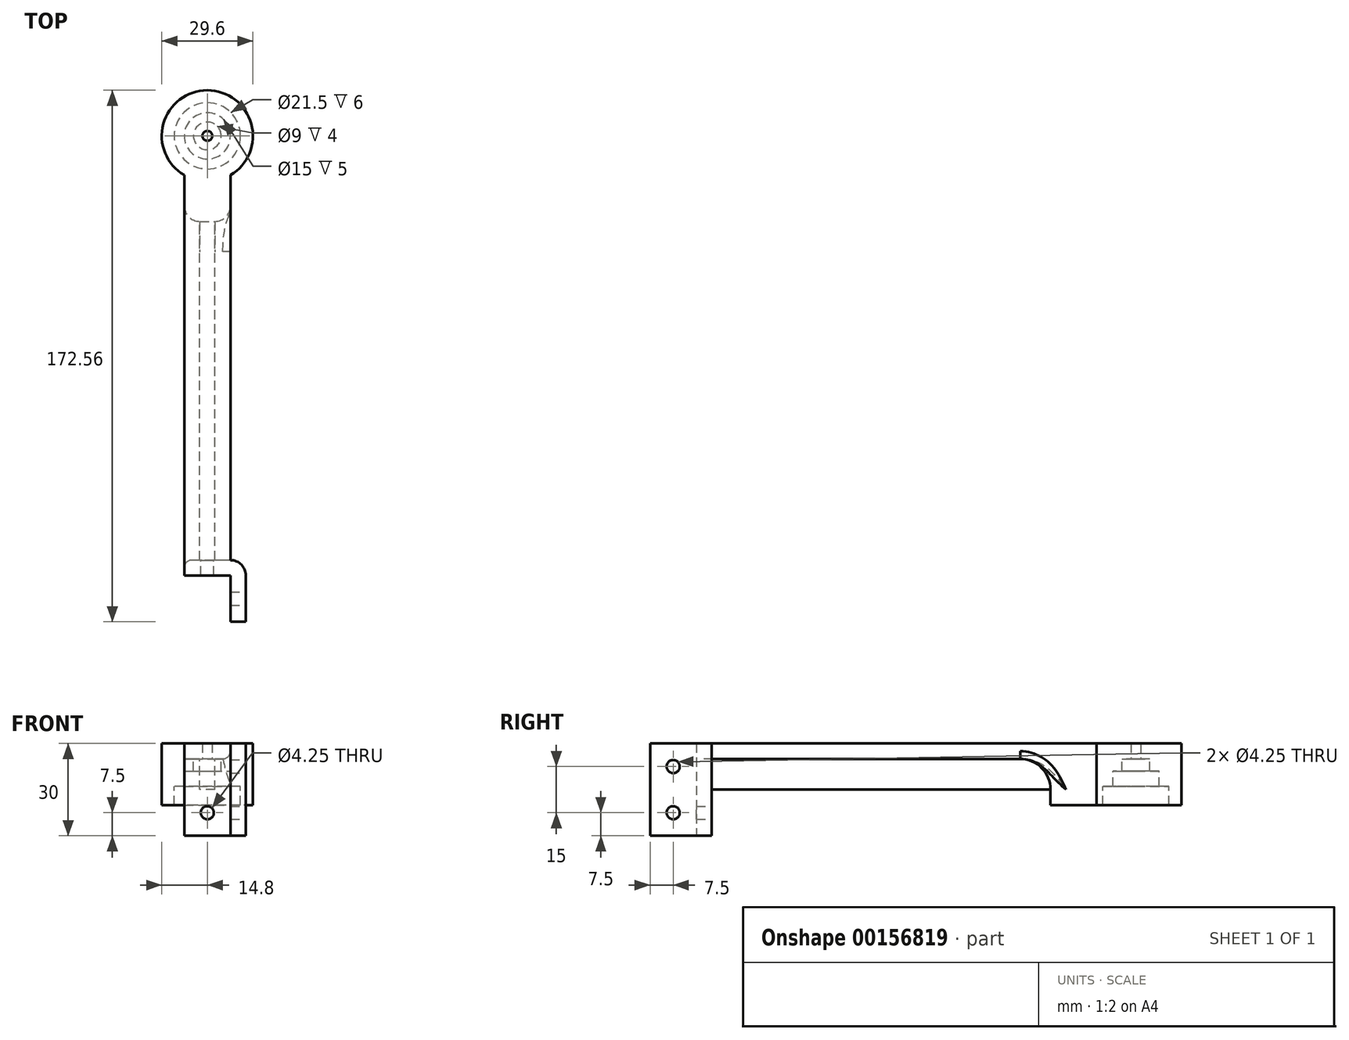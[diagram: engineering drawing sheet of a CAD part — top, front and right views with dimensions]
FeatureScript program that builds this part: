
annotation { "Feature Type Name" : "Feature", "Feature Type Description" : "" }
export const myFeature = defineFeature(function(context is Context, id is Id, definition is map)
    precondition{}
    {
        {
            var Q0;
            Q0=qCreatedBy(makeId("Top.planeOp"),FACE);
            var sketch = newSketch(context, id + "F0", { "sketchPlane" : qUnion([Q0])});
            skLineSegment(sketch, "E0.top", {"start": v(7.5, -65) * mm, "end": v(-7.5, -65) * mm});
            skLineSegment(sketch, "E0.left", {"start": v(7.5, 65) * mm, "end": v(7.5, -65) * mm});
            skLineSegment(sketch, "E0.right", {"start": v(-7.5, 65) * mm, "end": v(-7.5, -65) * mm});
            skPoint(sketch, "E0.middle", {"position": v(0, 0) * mm});
            skArc(sketch, "E1", {"start": v(10, 77.76) * mm, "mid": v(0, 67.76) * mm, "end": v(-10, 77.76) * mm, "construction": true});
            skArc(sketch, "E2", {"start": v(14.8, 77.76) * mm, "mid": v(12.85, 70.4) * mm, "end": v(7.5, 65) * mm});
            skArc(sketch, "E3.trimOffspring", {"start": v(-7.5, 65) * mm, "mid": v(-12.85, 70.4) * mm, "end": v(-14.8, 77.76) * mm});
            skArc(sketch, "E4", {"start": v(14.8, 77.76) * mm, "mid": v(0, 92.56) * mm, "end": v(-14.8, 77.76) * mm});
            skArc(sketch, "E5", {"start": v(10, 77.76) * mm, "mid": v(0, 87.76) * mm, "end": v(-10, 77.76) * mm, "construction": true});
            skCircle(sketch, "E6", {"center": v(0, 77.76) * mm, "radius": 1.6 * mm});
            skSolve(sketch);
        }
        {
            var Q0;
            Q0=qSketchRegion(id+"F0",true);
            extrude(context, id + "F1", {"entities" : qUnion([Q0]), "depth" : 5 * mm});
        }
        {
            var Q0;
            Q0=makeQuery(id+"F1.opExtrude","CAP_FACE",FACE,{"disambiguationData":[OSD([sQuery(id+"F0.wireOp",EDGE,"E0.top"),sQuery(id+"F0.wireOp",EDGE,"E0.left"),sQuery(id+"F0.wireOp",EDGE,"E0.right"),sQuery(id+"F0.wireOp",EDGE,"E1"),sQuery(id+"F0.wireOp",EDGE,"E2"),sQuery(id+"F0.wireOp",EDGE,"PIiDe5xE-f48K-SFec-VeXW-8BEBNLWFIkbi"),sQuery(id+"F0.wireOp",EDGE,"eIUL9qrP-yxCU-yPW2-WiAL-nEhhlfbeueWp"),sQuery(id+"F0.wireOp",EDGE,"NGNwJRk0-PCto-h1U5-63Ki-JEH3zZtKr13U"),sQuery(id+"F0.wireOp",EDGE,"9JBDCSfi-IbL8-SLhU-QHty-wRifAwfVzchu"),sQuery(id+"F0.wireOp",EDGE,"uUBvHsI4-013N-H5fo-1cTm-d3MeMkX9Puon"),sQuery(id+"F0.wireOp",EDGE,"XBA7hVCw-AGae-m0qZ-7ZIr-1CJPmpSNLz33"),sQuery(id+"F0.wireOp",EDGE,"E3.trimOffspring")])],"isStart":false});
            var sketch = newSketch(context, id + "F2", { "sketchPlane" : qUnion([Q0])});
            skLineSegment(sketch, "E7.bottom", {"start": v(2.5, -65) * mm, "end": v(-2.5, -65) * mm});
            skLineSegment(sketch, "E7.top", {"start": v(2.5, 65) * mm, "end": v(-2.5, 65) * mm});
            skLineSegment(sketch, "E7.left", {"start": v(2.5, -65) * mm, "end": v(2.5, 65) * mm});
            skLineSegment(sketch, "E7.right", {"start": v(-2.5, -65) * mm, "end": v(-2.5, 65) * mm});
            skPoint(sketch, "E7.middle", {"position": v(0, 0) * mm});
            skSolve(sketch);
        }
        {
            var Q0;
            Q0=qSketchRegion(id+"F2",true);
            extrude(context, id + "F3", {"entities" : qUnion([Q0]), "operationType" : NewBodyOperationType.ADD, "oppositeDirection" : true, "depth" : 15 * mm});
        }
        {
            var Q0;
            Q0=makeQuery(id+"F1.opExtrude","CAP_FACE",FACE,{"disambiguationData":[OSD([sQuery(id+"F0.wireOp",EDGE,"E0.top"),sQuery(id+"F0.wireOp",EDGE,"E0.left"),sQuery(id+"F0.wireOp",EDGE,"E0.right"),sQuery(id+"F0.wireOp",EDGE,"E2"),sQuery(id+"F0.wireOp",EDGE,"eIUL9qrP-yxCU-yPW2-WiAL-nEhhlfbeueWp"),sQuery(id+"F0.wireOp",EDGE,"NGNwJRk0-PCto-h1U5-63Ki-JEH3zZtKr13U"),sQuery(id+"F0.wireOp",EDGE,"uUBvHsI4-013N-H5fo-1cTm-d3MeMkX9Puon"),sQuery(id+"F0.wireOp",EDGE,"XBA7hVCw-AGae-m0qZ-7ZIr-1CJPmpSNLz33"),sQuery(id+"F0.wireOp",EDGE,"E3.trimOffspring"),sQuery(id+"F0.wireOp",EDGE,"dFs57Gag-QdQH-sll3-50n3-rowVGE8G3t0V")])],"isStart":false});
            var sketch = newSketch(context, id + "F4", { "sketchPlane" : qUnion([Q0])});
            skArc(sketch, "E8", {"start": v(-10.75, 77.76) * mm, "mid": v(0, 67) * mm, "end": v(10.75, 77.76) * mm});
            skArc(sketch, "E9", {"start": v(-14.8, 77.76) * mm, "mid": v(-12.85, 70.4) * mm, "end": v(-7.5, 65) * mm});
            skArc(sketch, "E10", {"start": v(14.8, 77.76) * mm, "mid": v(12.85, 70.4) * mm, "end": v(7.5, 65) * mm});
            skLineSegment(sketch, "E11", {"start": v(-7.5, 65) * mm, "end": v(-7.5, 50) * mm});
            skLineSegment(sketch, "E12", {"start": v(-7.5, 50) * mm, "end": v(7.5, 50) * mm});
            skLineSegment(sketch, "E13", {"start": v(7.5, 50) * mm, "end": v(7.5, 65) * mm});
            skArc(sketch, "E14", {"start": v(10.75, 77.76) * mm, "mid": v(0, 88.5) * mm, "end": v(-10.75, 77.76) * mm});
            skArc(sketch, "E15", {"start": v(-14.8, 77.76) * mm, "mid": v(0, 92.56) * mm, "end": v(14.8, 77.76) * mm});
            skSolve(sketch);
        }
        {
            var Q0;
            Q0=qSketchRegion(id+"F4",true);
            extrude(context, id + "F5", {"entities" : qUnion([Q0]), "operationType" : NewBodyOperationType.ADD, "oppositeDirection" : true, "depth" : 20 * mm});
        }
        {
            var Q0;
            Q0=qCreatedBy(makeId("Top.planeOp"),FACE);
            var sketch = newSketch(context, id + "F6", { "sketchPlane" : qUnion([Q0])});
            skLineSegment(sketch, "E16", {"start": v(-7.5, -65) * mm, "end": v(7.5, -65) * mm});
            skLineSegment(sketch, "E17", {"start": v(7.5, -65) * mm, "end": v(7.5, -80) * mm});
            skLineSegment(sketch, "E18", {"start": v(7.5, -80) * mm, "end": v(12.5, -80) * mm});
            skLineSegment(sketch, "E19", {"start": v(12.5, -80) * mm, "end": v(12.5, -65) * mm});
            skLineSegment(sketch, "E20", {"start": v(7.5, -60) * mm, "end": v(-7.5, -60) * mm});
            skLineSegment(sketch, "E21", {"start": v(-7.5, -60) * mm, "end": v(-7.5, -65) * mm});
            skPoint(sketch, "E22.visualSharp", {"position": v(12.5, -60) * mm});
            skArc(sketch, "E22.filletArc", {"start": v(12.5, -65) * mm, "mid": v(11.04, -61.46) * mm, "end": v(7.5, -60) * mm});
            skSolve(sketch);
        }
        {
            var Q0;
            Q0=qSketchRegion(id+"F6",true);
            extrude(context, id + "F7", {"entities" : qUnion([Q0]), "operationType" : NewBodyOperationType.ADD, "oppositeDirection" : true, "depth" : 25 * mm});
        }
        {
            var Q0;
            Q0=makeQuery(id+"F7.opExtrude","CAP_FACE",FACE,{"disambiguationData":[OSD([sQuery(id+"F6.wireOp",EDGE,"E16"),sQuery(id+"F6.wireOp",EDGE,"E17"),sQuery(id+"F6.wireOp",EDGE,"E18"),sQuery(id+"F6.wireOp",EDGE,"E19"),sQuery(id+"F6.wireOp",EDGE,"E20"),sQuery(id+"F6.wireOp",EDGE,"E21"),sQuery(id+"F6.wireOp",EDGE,"E22.filletArc")])],"isStart":true});
            var sketch = newSketch(context, id + "F8", { "sketchPlane" : qUnion([Q0])});
            skLineSegment(sketch, "E23", {"start": v(7.5, -60) * mm, "end": v(7.5, -80) * mm});
            skLineSegment(sketch, "E24", {"start": v(7.5, -80) * mm, "end": v(12.5, -80) * mm});
            skLineSegment(sketch, "E25", {"start": v(12.5, -80) * mm, "end": v(12.5, -65) * mm});
            skArc(sketch, "E26", {"start": v(12.5, -65) * mm, "mid": v(11.04, -61.46) * mm, "end": v(7.5, -60) * mm});
            skSolve(sketch);
        }
        {
            var Q0;
            Q0=qSketchRegion(id+"F8",true);
            extrude(context, id + "F9", {"entities" : qUnion([Q0]), "operationType" : NewBodyOperationType.ADD, "depth" : 5 * mm});
        }
        {
            var Q0;
            Q0=makeQuery(id+"F7.opExtrude","SWEPT_FACE",FACE,{"disambiguationData":[OSD([sQuery(id+"F6.wireOp",EDGE,"E19")])]});
            var sketch = newSketch(context, id + "F10", { "sketchPlane" : qUnion([Q0])});
            skCircle(sketch, "E27", {"center": v(-72.5, -17.5) * mm, "radius": 2.12 * mm});
            skCircle(sketch, "E28", {"center": v(-72.5, -2.5) * mm, "radius": 2.12 * mm});
            skSolve(sketch);
        }
        {
            var Q0;
            Q0=qSketchRegion(id+"F10",true);
            extrude(context, id + "F11", {"entities" : qUnion([Q0]), "operationType" : NewBodyOperationType.REMOVE, "endBound" : BoundingType.THROUGH_ALL, "oppositeDirection" : true, "depth" : 25 * mm});
        }
        {
            var Q0;
            Q0=makeQuery(id+"F7.boolean.opBoolean","INTERSECT",EDGE,{"derivedFrom":[makeQuery(id+"F5.boolean.opBoolean","MERGE",FACE,{"derivedFrom":[makeQuery(id+"F3.opExtrude","CAP_FACE",FACE,{"disambiguationData":[OSD([sQuery(id+"F2.wireOp",EDGE,"E7.bottom"),sQuery(id+"F2.wireOp",EDGE,"E7.top"),sQuery(id+"F2.wireOp",EDGE,"E7.left"),sQuery(id+"F2.wireOp",EDGE,"E7.right")])],"isStart":false}),makeQuery(id+"F5.opExtrude","CAP_FACE",FACE,{"disambiguationData":[OSD([sQuery(id+"F4.wireOp",EDGE,"cwlC9csa-SC08-sSLQ-h5yO-vNUKiVOiDg0u"),sQuery(id+"F4.wireOp",EDGE,"jy26kect-yQTE-EkO8-PW5k-TZuoNj3gaL8H"),sQuery(id+"F4.wireOp",EDGE,"58l5BIxD-UzrF-AVzm-vQBL-5cT0BnXlhkos"),sQuery(id+"F4.wireOp",EDGE,"kAuWynmu-Th3E-5vG2-5KpU-cPiFX5i8FIhA"),sQuery(id+"F4.wireOp",EDGE,"E8"),sQuery(id+"F4.wireOp",EDGE,"E9"),sQuery(id+"F4.wireOp",EDGE,"E10"),sQuery(id+"F4.wireOp",EDGE,"E11"),sQuery(id+"F4.wireOp",EDGE,"E12"),sQuery(id+"F4.wireOp",EDGE,"E13"),sQuery(id+"F4.wireOp",EDGE,"eND8sEMT-CXld-e3JR-2aoP-SbV8lDfwxVoI"),sQuery(id+"F4.wireOp",EDGE,"LuQfHn9Y-Tg6M-KeqH-ZfVC-w0qiiegcXc9s")])],"isStart":false})]}),makeQuery(id+"F7.opExtrude","SWEPT_FACE",FACE,{"disambiguationData":[OSD([sQuery(id+"F6.wireOp",EDGE,"E20")])]})]});
            var Q1;
            Q1=makeQuery(id+"F5.opExtrude","SWEPT_EDGE",EDGE,{"disambiguationData":[OSD([sQuery(id+"F0.wireOp",EDGE,"E0.left"),sQuery(id+"F4.wireOp",EDGE,"E12"),sQuery(id+"F4.wireOp",EDGE,"E13")])]});
            var Q2;
            Q2=makeQuery(id+"F5.opExtrude","SWEPT_EDGE",EDGE,{"disambiguationData":[OSD([sQuery(id+"F0.wireOp",EDGE,"E0.right"),sQuery(id+"F4.wireOp",EDGE,"E11"),sQuery(id+"F4.wireOp",EDGE,"E12")])]});
            fillet(context, id + "F12", {"entities" : qUnion([Q0, Q1, Q2]), "radius" : 5 * mm, "tangentPropagation" : true, "allowEdgeOverflow" : false});
        }
        {
            var Q0;
            Q0=makeQuery(id+"F7.opExtrude","SWEPT_FACE",FACE,{"disambiguationData":[OSD([sQuery(id+"F6.wireOp",EDGE,"E20")])]});
            var sketch = newSketch(context, id + "F13", { "sketchPlane" : qUnion([Q0])});
            skCircle(sketch, "E29", {"center": v(0, -17.5) * mm, "radius": 2.12 * mm});
            skSolve(sketch);
        }
        {
            var Q0;
            Q0=qSketchRegion(id+"F13",true);
            extrude(context, id + "F14", {"entities" : qUnion([Q0]), "operationType" : NewBodyOperationType.REMOVE, "endBound" : BoundingType.THROUGH_ALL, "oppositeDirection" : true, "depth" : 25 * mm});
        }
        {
            var Q0;
            {var subQ0=sQuery(id+"F0.wireOp",EDGE,"E0.right");var subQ1=sQuery(id+"F6.wireOp",EDGE,"E20");Q0=makeQuery(id+"F7.boolean.opBoolean","SPLIT",EDGE,{"disambiguationData":[TD([makeQuery(id+"F1.opExtrude","SWEPT_FACE",FACE,{"disambiguationData":[OSD([subQ0])]})])],"derivedFrom":makeQuery(id+"F7.opExtrude","CAP_EDGE",EDGE,{"disambiguationData":[OSD([subQ1])],"isStart":true})});}
            var Q1;
            {var subQ0=sQuery(id+"F0.wireOp",EDGE,"E0.left");var subQ1=sQuery(id+"F6.wireOp",EDGE,"E20");Q1=makeQuery(id+"F7.boolean.opBoolean","SPLIT",EDGE,{"disambiguationData":[TD([makeQuery(id+"F1.opExtrude","SWEPT_FACE",FACE,{"disambiguationData":[OSD([subQ0])]})])],"derivedFrom":makeQuery(id+"F7.opExtrude","CAP_EDGE",EDGE,{"disambiguationData":[OSD([subQ1])],"isStart":true})});}
            var Q2;
            {var subQ0=sQuery(id+"F0.wireOp",EDGE,"E0.right");var subQ1=sQuery(id+"F0.wireOp",EDGE,"E0.top");var subQ2=sQuery(id+"F4.wireOp",EDGE,"E11");var subQ3=sQuery(id+"F4.wireOp",EDGE,"E12");Q2=makeQuery(id+"F12.opFillet","BLEND_EDGE",EDGE,{"blendedFrom":[makeQuery(id+"F5.opExtrude","SWEPT_EDGE",EDGE,{"disambiguationData":[OSD([subQ0,subQ2,subQ3])]}),makeQuery(id+"F5.boolean.opBoolean","SPLIT",FACE,{"disambiguationData":[TD([makeQuery(id+"F1.opExtrude","SWEPT_FACE",FACE,{"disambiguationData":[OSD([subQ0])]})])],"derivedFrom":makeQuery(id+"F1.opExtrude","CAP_FACE",FACE,{"disambiguationData":[OSD([subQ1,sQuery(id+"F0.wireOp",EDGE,"E0.left"),subQ0,sQuery(id+"F0.wireOp",EDGE,"E1"),sQuery(id+"F0.wireOp",EDGE,"E2"),sQuery(id+"F0.wireOp",EDGE,"PIiDe5xE-f48K-SFec-VeXW-8BEBNLWFIkbi"),sQuery(id+"F0.wireOp",EDGE,"eIUL9qrP-yxCU-yPW2-WiAL-nEhhlfbeueWp"),sQuery(id+"F0.wireOp",EDGE,"NGNwJRk0-PCto-h1U5-63Ki-JEH3zZtKr13U"),sQuery(id+"F0.wireOp",EDGE,"9JBDCSfi-IbL8-SLhU-QHty-wRifAwfVzchu"),sQuery(id+"F0.wireOp",EDGE,"uUBvHsI4-013N-H5fo-1cTm-d3MeMkX9Puon"),sQuery(id+"F0.wireOp",EDGE,"XBA7hVCw-AGae-m0qZ-7ZIr-1CJPmpSNLz33"),sQuery(id+"F0.wireOp",EDGE,"E3.trimOffspring")])],"isStart":true})})],"blendedInto":[makeQuery(id+"F5.boolean.opBoolean","SPLIT",FACE,{"disambiguationData":[TD([makeQuery(id+"F1.opExtrude","SWEPT_FACE",FACE,{"disambiguationData":[OSD([subQ0])]})])],"derivedFrom":makeQuery(id+"F1.opExtrude","CAP_FACE",FACE,{"disambiguationData":[OSD([subQ1,sQuery(id+"F0.wireOp",EDGE,"E0.left"),subQ0,sQuery(id+"F0.wireOp",EDGE,"E1"),sQuery(id+"F0.wireOp",EDGE,"E2"),sQuery(id+"F0.wireOp",EDGE,"PIiDe5xE-f48K-SFec-VeXW-8BEBNLWFIkbi"),sQuery(id+"F0.wireOp",EDGE,"eIUL9qrP-yxCU-yPW2-WiAL-nEhhlfbeueWp"),sQuery(id+"F0.wireOp",EDGE,"NGNwJRk0-PCto-h1U5-63Ki-JEH3zZtKr13U"),sQuery(id+"F0.wireOp",EDGE,"9JBDCSfi-IbL8-SLhU-QHty-wRifAwfVzchu"),sQuery(id+"F0.wireOp",EDGE,"uUBvHsI4-013N-H5fo-1cTm-d3MeMkX9Puon"),sQuery(id+"F0.wireOp",EDGE,"XBA7hVCw-AGae-m0qZ-7ZIr-1CJPmpSNLz33"),sQuery(id+"F0.wireOp",EDGE,"E3.trimOffspring")])],"isStart":true})})]});}
            var Q3;
            {var subQ0=sQuery(id+"F4.wireOp",EDGE,"E13");var subQ1=sQuery(id+"F0.wireOp",EDGE,"E0.left");var subQ2=sQuery(id+"F0.wireOp",EDGE,"E0.top");var subQ3=sQuery(id+"F4.wireOp",EDGE,"E12");Q3=makeQuery(id+"F12.opFillet","BLEND_EDGE",EDGE,{"blendedFrom":[makeQuery(id+"F5.opExtrude","SWEPT_EDGE",EDGE,{"disambiguationData":[OSD([subQ1,subQ3,subQ0])]}),makeQuery(id+"F5.boolean.opBoolean","SPLIT",FACE,{"disambiguationData":[TD([makeQuery(id+"F1.opExtrude","SWEPT_FACE",FACE,{"disambiguationData":[OSD([subQ1])]})])],"derivedFrom":makeQuery(id+"F1.opExtrude","CAP_FACE",FACE,{"disambiguationData":[OSD([subQ2,subQ1,sQuery(id+"F0.wireOp",EDGE,"E0.right"),sQuery(id+"F0.wireOp",EDGE,"E1"),sQuery(id+"F0.wireOp",EDGE,"E2"),sQuery(id+"F0.wireOp",EDGE,"PIiDe5xE-f48K-SFec-VeXW-8BEBNLWFIkbi"),sQuery(id+"F0.wireOp",EDGE,"eIUL9qrP-yxCU-yPW2-WiAL-nEhhlfbeueWp"),sQuery(id+"F0.wireOp",EDGE,"NGNwJRk0-PCto-h1U5-63Ki-JEH3zZtKr13U"),sQuery(id+"F0.wireOp",EDGE,"9JBDCSfi-IbL8-SLhU-QHty-wRifAwfVzchu"),sQuery(id+"F0.wireOp",EDGE,"uUBvHsI4-013N-H5fo-1cTm-d3MeMkX9Puon"),sQuery(id+"F0.wireOp",EDGE,"XBA7hVCw-AGae-m0qZ-7ZIr-1CJPmpSNLz33"),sQuery(id+"F0.wireOp",EDGE,"E3.trimOffspring")])],"isStart":true})})],"blendedInto":[makeQuery(id+"F5.boolean.opBoolean","SPLIT",FACE,{"disambiguationData":[TD([makeQuery(id+"F1.opExtrude","SWEPT_FACE",FACE,{"disambiguationData":[OSD([subQ1])]})])],"derivedFrom":makeQuery(id+"F1.opExtrude","CAP_FACE",FACE,{"disambiguationData":[OSD([subQ2,subQ1,sQuery(id+"F0.wireOp",EDGE,"E0.right"),sQuery(id+"F0.wireOp",EDGE,"E1"),sQuery(id+"F0.wireOp",EDGE,"E2"),sQuery(id+"F0.wireOp",EDGE,"PIiDe5xE-f48K-SFec-VeXW-8BEBNLWFIkbi"),sQuery(id+"F0.wireOp",EDGE,"eIUL9qrP-yxCU-yPW2-WiAL-nEhhlfbeueWp"),sQuery(id+"F0.wireOp",EDGE,"NGNwJRk0-PCto-h1U5-63Ki-JEH3zZtKr13U"),sQuery(id+"F0.wireOp",EDGE,"9JBDCSfi-IbL8-SLhU-QHty-wRifAwfVzchu"),sQuery(id+"F0.wireOp",EDGE,"uUBvHsI4-013N-H5fo-1cTm-d3MeMkX9Puon"),sQuery(id+"F0.wireOp",EDGE,"XBA7hVCw-AGae-m0qZ-7ZIr-1CJPmpSNLz33"),sQuery(id+"F0.wireOp",EDGE,"E3.trimOffspring")])],"isStart":true})})]});}
            fillet(context, id + "F15", {"entities" : qUnion([Q0, Q1, Q2, Q3]), "radius" : 10 * mm, "tangentPropagation" : true, "allowEdgeOverflow" : false});
        }
        {
            var Q0;
            Q0=makeQuery(id+"F7.opExtrude","SWEPT_EDGE",EDGE,{"disambiguationData":[OSD([sQuery(id+"F6.wireOp",EDGE,"E20"),sQuery(id+"F6.wireOp",EDGE,"E21")])]});
            var Q1;
            {var subQ0=sQuery(id+"F0.wireOp",EDGE,"E0.left");Q1=makeQuery(id+"F7.boolean.opBoolean","SPLIT",EDGE,{"disambiguationData":[TD([makeQuery(id+"F5.opExtrude","SWEPT_FACE",FACE,{"disambiguationData":[OSD([sQuery(id+"F4.wireOp",EDGE,"E12")])]})])],"derivedFrom":makeQuery(id+"F1.opExtrude","CAP_EDGE",EDGE,{"disambiguationData":[OSD([subQ0])],"isStart":true})});}
            fillet(context, id + "F16", {"entities" : qUnion([Q0, Q1]), "radius" : 2.5 * mm, "tangentPropagation" : true, "allowEdgeOverflow" : false});
        }
        {
            var Q0;
            {var subQ0=sQuery(id+"F0.wireOp",EDGE,"E6");Q0=makeQuery(id+"F5.boolean.opBoolean","SPLIT",FACE,{"disambiguationData":[TD([makeQuery(id+"F1.opExtrude","SWEPT_FACE",FACE,{"disambiguationData":[OSD([subQ0])]})])],"derivedFrom":makeQuery(id+"F1.opExtrude","CAP_FACE",FACE,{"disambiguationData":[OSD([sQuery(id+"F0.wireOp",EDGE,"E0.top"),sQuery(id+"F0.wireOp",EDGE,"E0.left"),sQuery(id+"F0.wireOp",EDGE,"E0.right"),sQuery(id+"F0.wireOp",EDGE,"E2"),sQuery(id+"F0.wireOp",EDGE,"E3.trimOffspring"),sQuery(id+"F0.wireOp",EDGE,"E4"),subQ0])],"isStart":true})});}
            var sketch = newSketch(context, id + "F17", { "sketchPlane" : qUnion([Q0])});
            skCircle(sketch, "E30", {"center": v(0, -77.76) * mm, "radius": 4.5 * mm});
            skCircle(sketch, "E31", {"center": v(0, -77.76) * mm, "radius": 10.75 * mm});
            skSolve(sketch);
        }
        {
            var Q0;
            Q0=qSketchRegion(id+"F17",true);
            extrude(context, id + "F18", {"entities" : qUnion([Q0]), "operationType" : NewBodyOperationType.ADD, "depth" : 4 * mm});
        }
        {
            var Q0;
            Q0=makeQuery(id+"F18.opExtrude","CAP_FACE",FACE,{"disambiguationData":[OSD([sQuery(id+"F17.wireOp",EDGE,"E30"),sQuery(id+"F17.wireOp",EDGE,"E31")])],"isStart":false});
            var sketch = newSketch(context, id + "F19", { "sketchPlane" : qUnion([Q0])});
            skCircle(sketch, "E32", {"center": v(0, -77.76) * mm, "radius": 7.5 * mm});
            skCircle(sketch, "E33", {"center": v(0, -77.76) * mm, "radius": 10.75 * mm});
            skSolve(sketch);
        }
        {
            var Q0;
            Q0=qSketchRegion(id+"F19",true);
            extrude(context, id + "F20", {"entities" : qUnion([Q0]), "operationType" : NewBodyOperationType.ADD, "depth" : 5 * mm});
        }
    });
